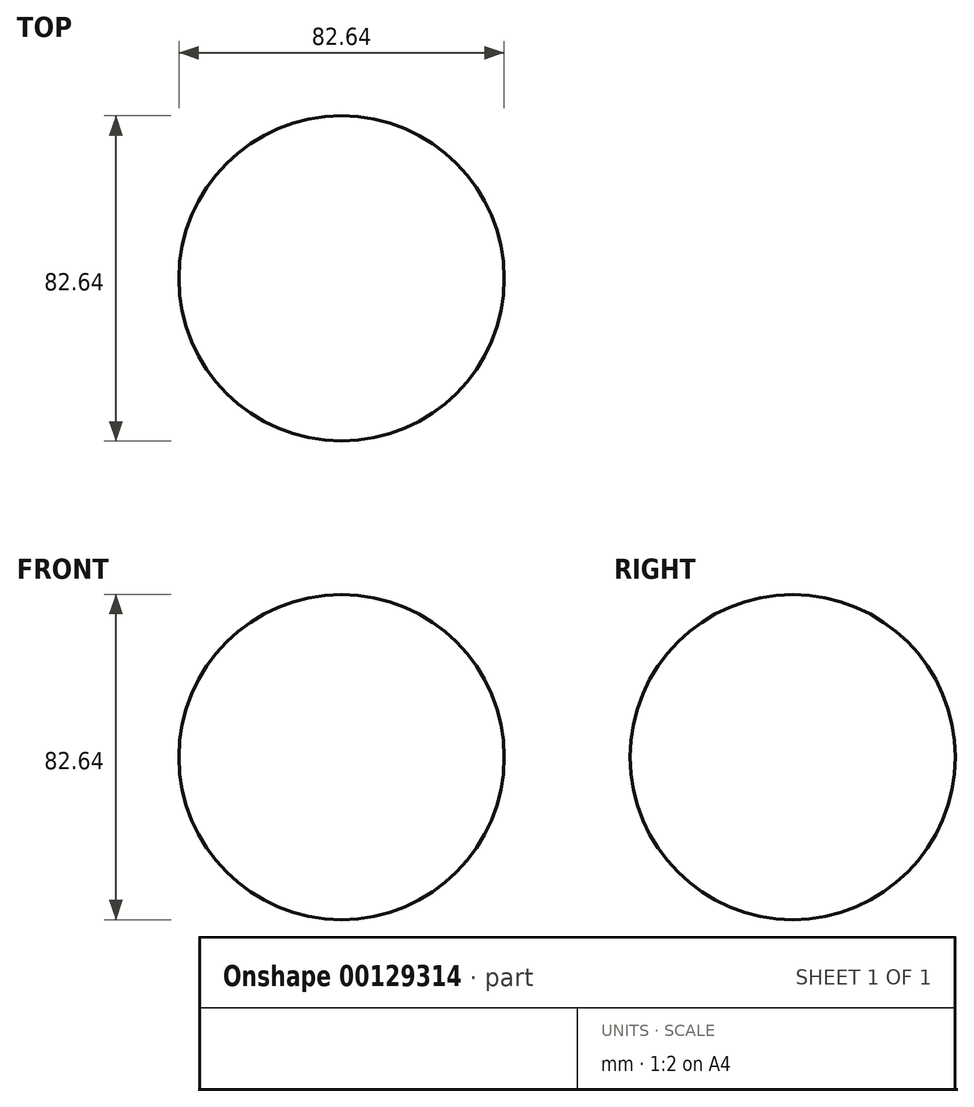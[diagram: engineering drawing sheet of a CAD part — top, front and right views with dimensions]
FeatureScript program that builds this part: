
annotation { "Feature Type Name" : "Feature", "Feature Type Description" : "" }
export const myFeature = defineFeature(function(context is Context, id is Id, definition is map)
    precondition{}
    {
        {
            var Q0;
            Q0=qCreatedBy(makeId("Front.planeOp"),FACE);
            var sketch = newSketch(context, id + "F0", { "sketchPlane" : qUnion([Q0])});
            skCircle(sketch, "E0", {"center": v(0, 0) * mm, "radius": 41.32 * mm});
            skLineSegment(sketch, "E1", {"start": v(0, 41.32) * mm, "end": v(0, -41.32) * mm});
            skSolve(sketch);
        }
        {
            var Q0;
            {var subQ0=sQuery(id+"F0.wireOp",EDGE,"E1");Q0=makeQuery(id+"F0.imprint","IMPRINT",FACE,{"disambiguationData":[TD([[makeQuery(id+"F0.imprint","IMPRINT",EDGE,{"derivedFrom":subQ0}),-1.0]])]});}
            var Q1;
            Q1=sQuery(id+"F0.wireOp",EDGE,"E1");
            revolve(context, id + "F1", {"entities" : qUnion([Q0]), "axis" : qUnion([Q1]), "revolveType" : RevolveType.FULL});
        }
    });
